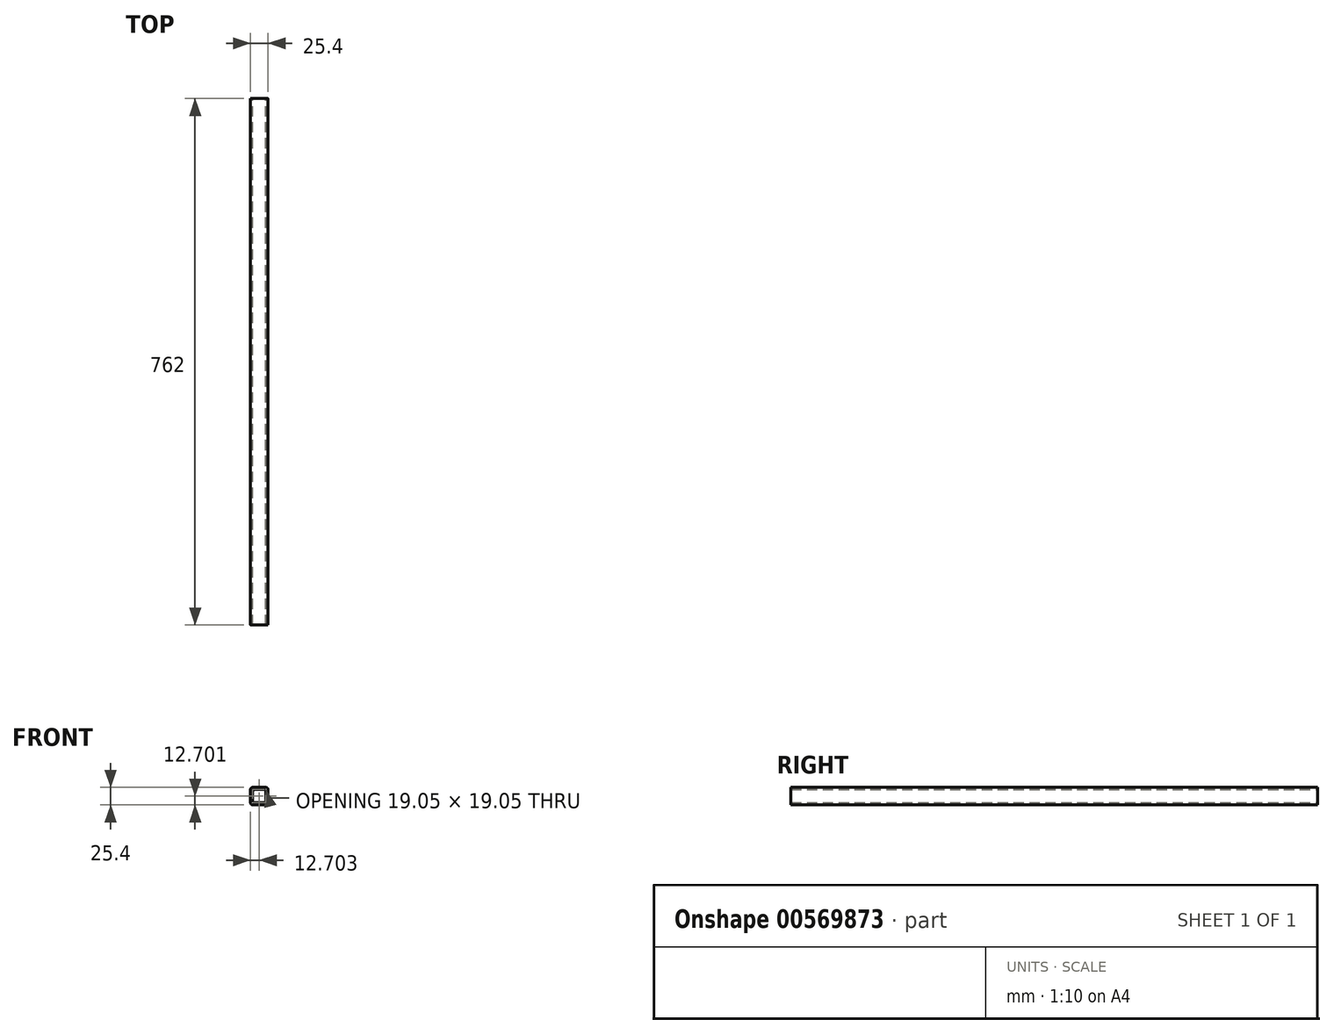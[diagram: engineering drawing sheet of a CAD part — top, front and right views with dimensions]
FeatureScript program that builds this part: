
annotation { "Feature Type Name" : "Feature", "Feature Type Description" : "" }
export const myFeature = defineFeature(function(context is Context, id is Id, definition is map)
    precondition{}
    {
        {
            var Q0;
            Q0=qCreatedBy(makeId("Front.planeOp"),FACE);
            var sketch = newSketch(context, id + "F0", { "sketchPlane" : qUnion([Q0])});
            skLineSegment(sketch, "E0.bottom", {"start": v(9.92, -12.2) * mm, "end": v(-9.13, -12.2) * mm});
            skLineSegment(sketch, "E0.top", {"start": v(9.92, 13.2) * mm, "end": v(-9.13, 13.2) * mm});
            skLineSegment(sketch, "E0.left", {"start": v(13.1, -9.03) * mm, "end": v(13.1, 10.02) * mm});
            skLineSegment(sketch, "E0.right", {"start": v(-12.3, -9.03) * mm, "end": v(-12.3, 10.02) * mm});
            skLineSegment(sketch, "E1.bottom", {"start": v(6.74, -9.03) * mm, "end": v(-5.96, -9.03) * mm});
            skLineSegment(sketch, "E1.top", {"start": v(6.74, 10.02) * mm, "end": v(-5.96, 10.02) * mm});
            skLineSegment(sketch, "E1.left", {"start": v(9.92, -5.86) * mm, "end": v(9.92, 6.84) * mm});
            skLineSegment(sketch, "E1.right", {"start": v(-9.13, -5.86) * mm, "end": v(-9.13, 6.84) * mm});
            skPoint(sketch, "E2.visualSharp", {"position": v(9.92, 10.02) * mm});
            skArc(sketch, "E2.filletArc", {"start": v(9.92, 6.84) * mm, "mid": v(8.99, 9.09) * mm, "end": v(6.74, 10.02) * mm});
            skPoint(sketch, "E3.visualSharp", {"position": v(-9.13, 10.02) * mm});
            skArc(sketch, "E3.filletArc", {"start": v(-5.96, 10.02) * mm, "mid": v(-8.2, 9.09) * mm, "end": v(-9.13, 6.84) * mm});
            skPoint(sketch, "E4.visualSharp", {"position": v(-9.13, -9.03) * mm});
            skArc(sketch, "E4.filletArc", {"start": v(-9.13, -5.86) * mm, "mid": v(-8.2, -8.1) * mm, "end": v(-5.96, -9.03) * mm});
            skPoint(sketch, "E5.visualSharp", {"position": v(9.92, -9.03) * mm});
            skArc(sketch, "E5.filletArc", {"start": v(6.74, -9.03) * mm, "mid": v(8.99, -8.1) * mm, "end": v(9.92, -5.86) * mm});
            skPoint(sketch, "E6.visualSharp", {"position": v(13.1, 13.2) * mm});
            skArc(sketch, "E6.filletArc", {"start": v(13.1, 10.02) * mm, "mid": v(12.16, 12.26) * mm, "end": v(9.92, 13.2) * mm});
            skPoint(sketch, "E7.visualSharp", {"position": v(-12.3, 13.2) * mm});
            skArc(sketch, "E7.filletArc", {"start": v(-9.13, 13.2) * mm, "mid": v(-11.38, 12.26) * mm, "end": v(-12.3, 10.02) * mm});
            skPoint(sketch, "E8.visualSharp", {"position": v(-12.3, -12.2) * mm});
            skArc(sketch, "E8.filletArc", {"start": v(-12.3, -9.03) * mm, "mid": v(-11.38, -11.28) * mm, "end": v(-9.13, -12.2) * mm});
            skPoint(sketch, "E9.visualSharp", {"position": v(13.1, -12.2) * mm});
            skArc(sketch, "E9.filletArc", {"start": v(9.92, -12.2) * mm, "mid": v(12.16, -11.28) * mm, "end": v(13.1, -9.03) * mm});
            skSolve(sketch);
        }
        {
            var Q0;
            Q0 = qSketchRegion(id + "F0", true);
            extrude(context, id + "F1", {"entities" : qUnion([Q0]), "depth" : 762 * mm, "offsetDistance" : 25.4 * mm});
        }
    });
